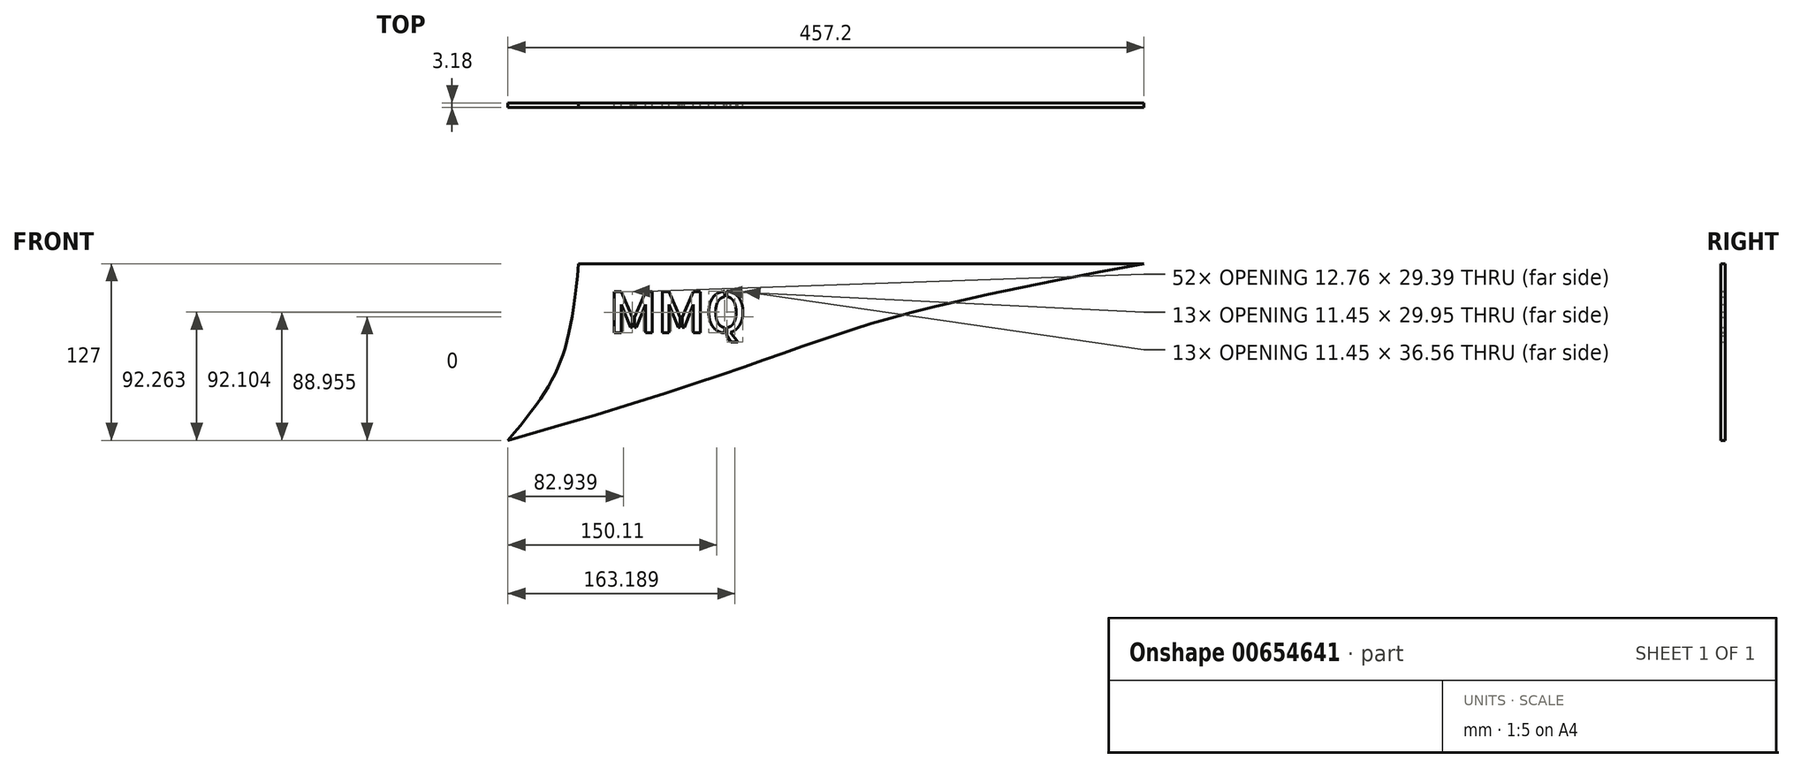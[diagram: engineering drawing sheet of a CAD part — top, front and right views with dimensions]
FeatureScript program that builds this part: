
annotation { "Feature Type Name" : "Feature", "Feature Type Description" : "" }
export const myFeature = defineFeature(function(context is Context, id is Id, definition is map)
    precondition{}
    {
        {
            var Q0;
            Q0=qCreatedBy(makeId("Front.planeOp"),FACE);
            var sketch = newSketch(context, id + "F0", { "sketchPlane" : qUnion([Q0])});
            skLineSegment(sketch, "E0", {"start": v(268.05, 49.6) * mm, "end": v(-138.35, 49.6) * mm});
            skLineSegment(sketch, "E1", {"start": v(-189.15, -77.4) * mm, "end": v(-189.15, -77.4) * mm});
            skFitSpline(sketch, "E2", {"points": [v(-138.35, 49.6) * mm, v(-189.15, -77.4) * mm], "startDerivative": vector(-19.19, -205.15) * mm, "endDerivative": vector(-110.51, -132.27) * mm});
            skFitSpline(sketch, "E3", {"points": [v(268.05, 49.6) * mm, v(-189.15, -77.4) * mm], "startDerivative": vector(-804.14, -148.77) * mm, "endDerivative": vector(-814.42, -232.23) * mm});
            skText(sketch, "E4", { "text": "MMQ", "fontName": "AllertaStencil-Regular.ttf"});
            const initialGuessF0  = {"E4": [-0.11626, 0, 1, 0, 0.0294]};
            skSetInitialGuess(sketch, initialGuessF0);
            skSolve(sketch);
        }
        {
            var Q0;
            Q0=makeQuery(id+"F0.imprint","IMPRINT",FACE,{"disambiguationData":[TD([[makeQuery(id+"F0.imprint","IMPRINT",EDGE,{"derivedFrom":sQuery(id+"F0.wireOp",EDGE,"E0")}),1.0]])]});
            extrude(context, id + "F1", {"entities" : qUnion([Q0]), "depth" : 3.17 * mm, "offsetDistance" : 25.4 * mm});
        }
    });
